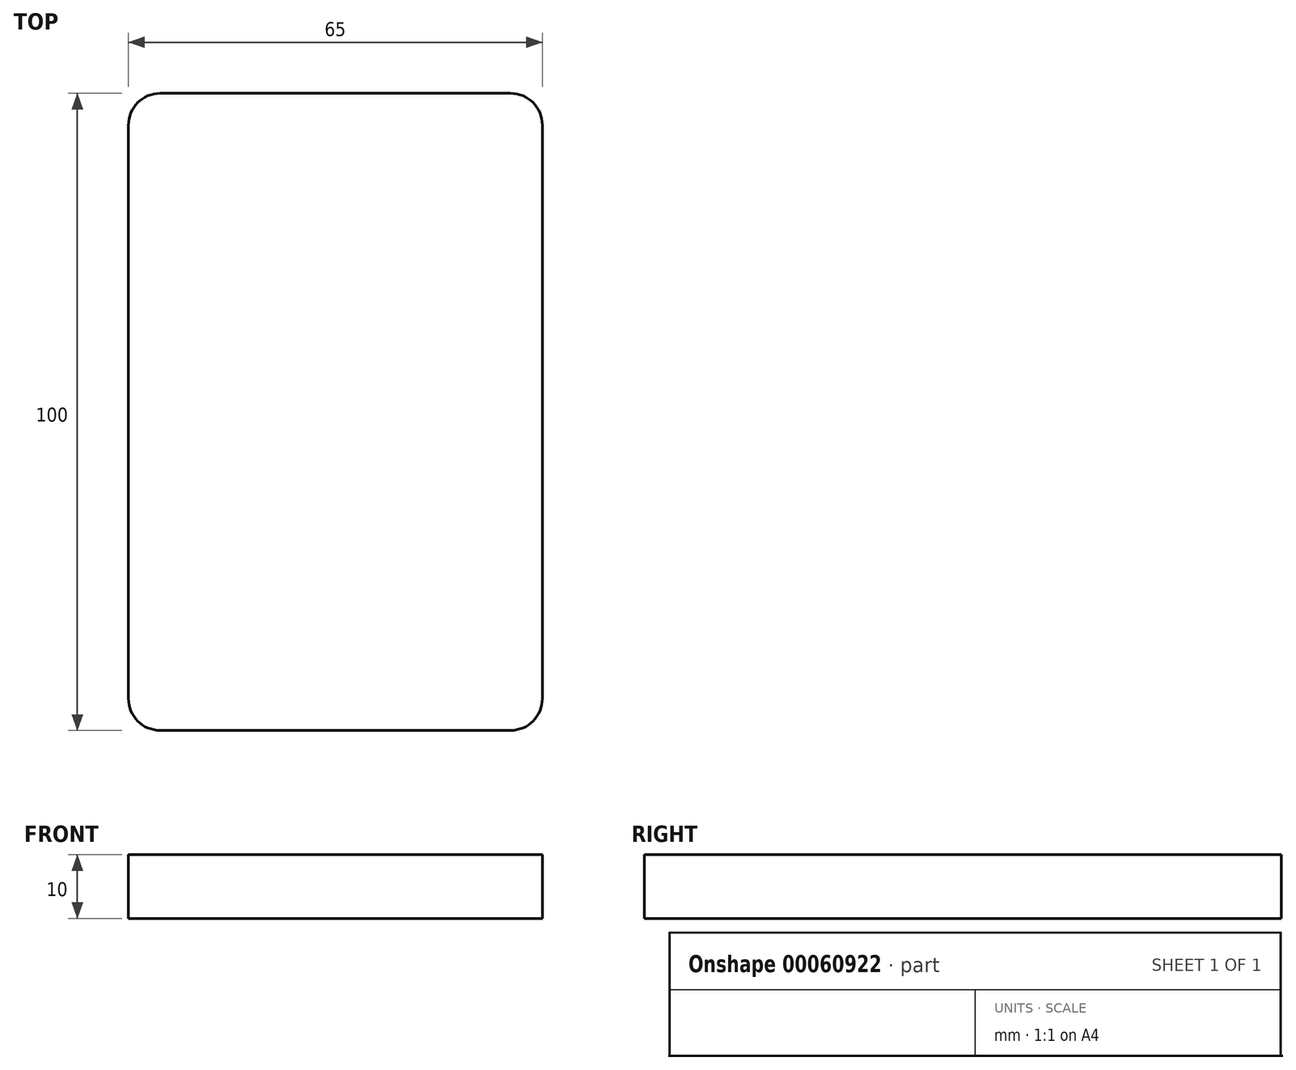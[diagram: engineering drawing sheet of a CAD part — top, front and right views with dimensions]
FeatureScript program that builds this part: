
annotation { "Feature Type Name" : "Feature", "Feature Type Description" : "" }
export const myFeature = defineFeature(function(context is Context, id is Id, definition is map)
    precondition{}
    {
        {
            assignVariable(context, id + "F0", {"name" : "trayDepth", "anyValue" : 10});
        }
        {
            var Q0;
            Q0=qCreatedBy(makeId("Top.planeOp"),FACE);
            var sketch = newSketch(context, id + "F1", { "sketchPlane" : qUnion([Q0])});
            skLineSegment(sketch, "E0.rect.bottom", {"start": v(-27.5, 50) * mm, "end": v(27.5, 50) * mm});
            skLineSegment(sketch, "E0.rect.top", {"start": v(-27.5, -50) * mm, "end": v(27.5, -50) * mm});
            skLineSegment(sketch, "E0.rect.left", {"start": v(-32.5, 45) * mm, "end": v(-32.5, -45) * mm});
            skLineSegment(sketch, "E0.rect.right", {"start": v(32.5, 45) * mm, "end": v(32.5, -45) * mm});
            skPoint(sketch, "E0.rect.middle", {"position": v(0, 0) * mm});
            skPoint(sketch, "E1.visualSharp", {"position": v(-32.5, 50) * mm});
            skArc(sketch, "E1.filletArc", {"start": v(-27.5, 50) * mm, "mid": v(-31.04, 48.54) * mm, "end": v(-32.5, 45) * mm});
            skPoint(sketch, "E2.visualSharp", {"position": v(32.5, 50) * mm});
            skArc(sketch, "E2.filletArc", {"start": v(32.5, 45) * mm, "mid": v(31.04, 48.54) * mm, "end": v(27.5, 50) * mm});
            skPoint(sketch, "E3.visualSharp", {"position": v(32.5, -50) * mm});
            skArc(sketch, "E3.filletArc", {"start": v(27.5, -50) * mm, "mid": v(31.04, -48.54) * mm, "end": v(32.5, -45) * mm});
            skPoint(sketch, "E4.visualSharp", {"position": v(-32.5, -50) * mm});
            skArc(sketch, "E4.filletArc", {"start": v(-32.5, -45) * mm, "mid": v(-31.04, -48.54) * mm, "end": v(-27.5, -50) * mm});
            skSolve(sketch);
        }
        {
            var Q0;
            Q0 = qSketchRegion(id + "F1", true);
            extrude(context, id + "F2", {"entities" : qUnion([Q0]), "depth" : (getVariable(context, 'trayDepth')) * mm});
        }
    });
